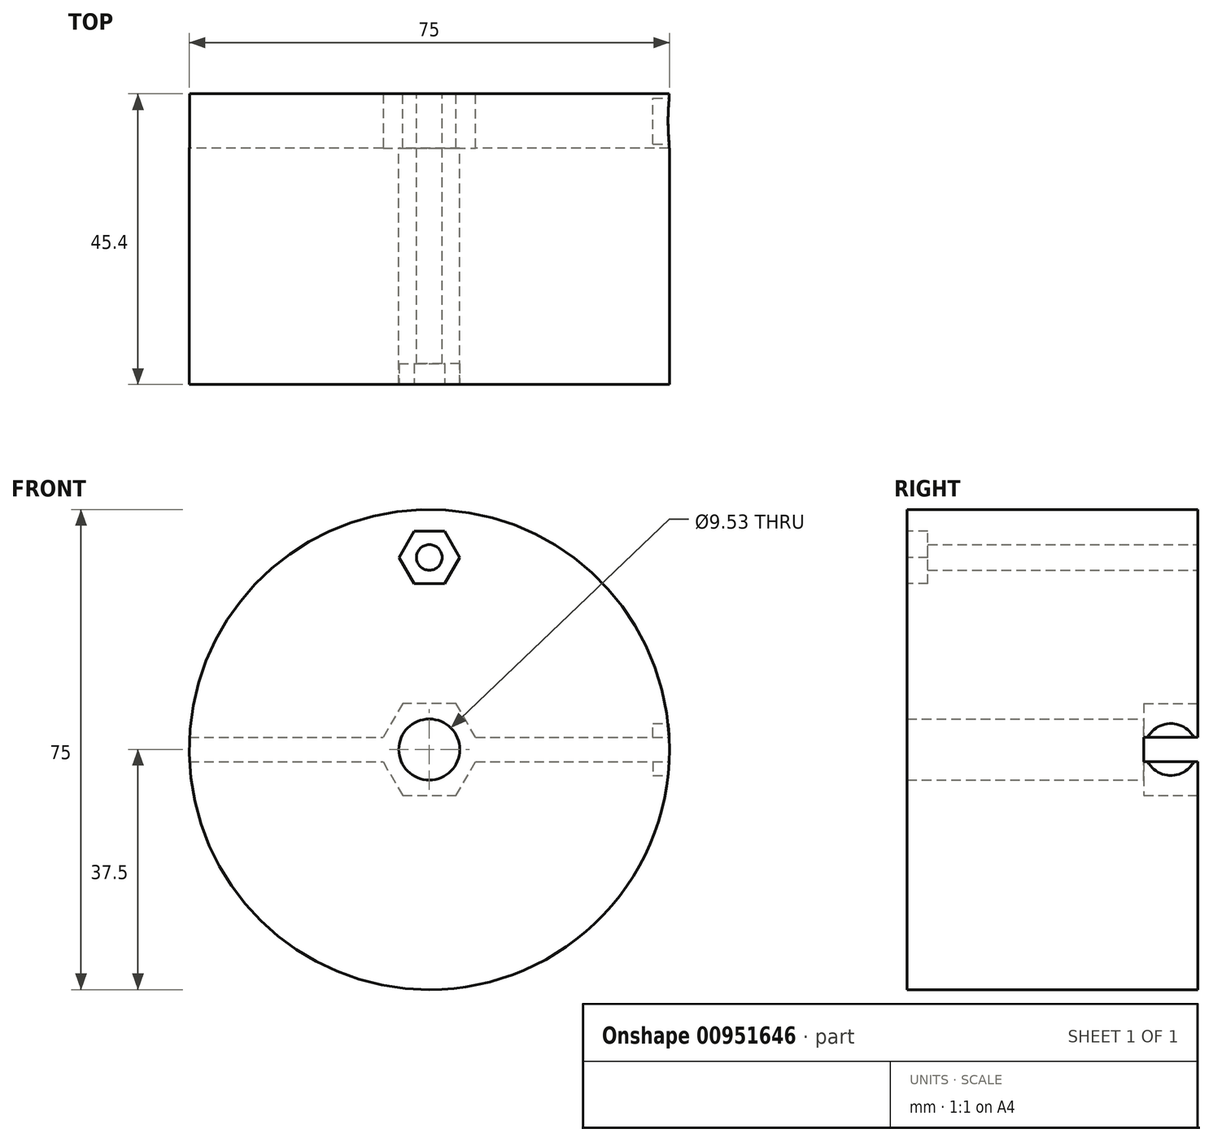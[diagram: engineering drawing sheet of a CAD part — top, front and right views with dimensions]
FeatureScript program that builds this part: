
annotation { "Feature Type Name" : "Feature", "Feature Type Description" : "" }
export const myFeature = defineFeature(function(context is Context, id is Id, definition is map)
    precondition{}
    {
        {
            var Q0;
            Q0=qCreatedBy(makeId("Front.planeOp"),FACE);
            var sketch = newSketch(context, id + "F0", { "sketchPlane" : qUnion([Q0])});
            skCircle(sketch, "E0", {"center": v(0, 0) * mm, "radius": 37.5 * mm});
            skSolve(sketch);
        }
        {
            var Q0;
            Q0=qSketchRegion(id+"F0",true);
            extrude(context, id + "F1", {"entities" : qUnion([Q0]), "depth" : 45.4 * mm, "offsetDistance" : 25 * mm});
        }
        {
            var Q0;
            Q0=qCreatedBy(makeId("Front.planeOp"),FACE);
            var sketch = newSketch(context, id + "F2", { "sketchPlane" : qUnion([Q0])});
            skCircle(sketch, "E1", {"center": v(0, 30) * mm, "radius": 2 * mm});
            skSolve(sketch);
        }
        {
            var Q0;
            Q0=qSketchRegion(id+"F2",true);
            extrude(context, id + "F3", {"entities" : qUnion([Q0]), "operationType" : NewBodyOperationType.REMOVE, "endBound" : BoundingType.THROUGH_ALL, "depth" : 25 * mm, "offsetDistance" : 25 * mm});
        }
        {
            var Q0;
            Q0=makeQuery(id+"F1.opExtrude","CAP_FACE",FACE,{"disambiguationData":[OSD([sQuery(id+"F0.wireOp",EDGE,"E0")])],"isStart":false});
            var sketch = newSketch(context, id + "F4", { "sketchPlane" : qUnion([Q0])});
            skCircle(sketch, "E2.cCircle", {"center": v(0, 30) * mm, "radius": 4.11 * mm, "construction": true});
            skLineSegment(sketch, "E2.0", {"start": v(-2.37, 34.11) * mm, "end": v(2.37, 34.11) * mm});
            skLineSegment(sketch, "E2.1", {"start": v(2.37, 34.11) * mm, "end": v(4.75, 30) * mm});
            skLineSegment(sketch, "E2.2", {"start": v(4.75, 30) * mm, "end": v(2.37, 25.89) * mm});
            skLineSegment(sketch, "E2.3", {"start": v(2.37, 25.89) * mm, "end": v(-2.37, 25.89) * mm});
            skLineSegment(sketch, "E2.4", {"start": v(-2.37, 25.89) * mm, "end": v(-4.75, 30) * mm});
            skLineSegment(sketch, "E2.5", {"start": v(-4.75, 30) * mm, "end": v(-2.37, 34.11) * mm});
            skPoint(sketch, "E2.0.midPoint", {"position": v(0, 34.11) * mm});
            skSolve(sketch);
        }
        {
            var Q0;
            Q0=qSketchRegion(id+"F4",true);
            extrude(context, id + "F5", {"entities" : qUnion([Q0]), "operationType" : NewBodyOperationType.REMOVE, "oppositeDirection" : true, "depth" : 3.25 * mm, "offsetDistance" : 25 * mm});
        }
        {
            var Q0;
            Q0=makeQuery(id+"F1.opExtrude","CAP_FACE",FACE,{"disambiguationData":[OSD([sQuery(id+"F0.wireOp",EDGE,"E0")])],"isStart":true});
            var sketch = newSketch(context, id + "F6", { "sketchPlane" : qUnion([Q0])});
            skCircle(sketch, "E3.cCircle", {"center": v(0, 0) * mm, "radius": 7.2 * mm, "construction": true});
            skLineSegment(sketch, "E3.0", {"start": v(4.16, -7.2) * mm, "end": v(-4.16, -7.2) * mm});
            skLineSegment(sketch, "E3.1", {"start": v(-4.16, -7.2) * mm, "end": v(-8.31, 0) * mm});
            skLineSegment(sketch, "E3.2", {"start": v(-8.31, 0) * mm, "end": v(-4.16, 7.2) * mm});
            skLineSegment(sketch, "E3.3", {"start": v(-4.16, 7.2) * mm, "end": v(4.16, 7.2) * mm});
            skLineSegment(sketch, "E3.4", {"start": v(4.16, 7.2) * mm, "end": v(8.31, 0) * mm});
            skLineSegment(sketch, "E3.5", {"start": v(8.31, 0) * mm, "end": v(4.16, -7.2) * mm});
            skPoint(sketch, "E3.0.midPoint", {"position": v(0, -7.2) * mm});
            skSolve(sketch);
        }
        {
            var Q0;
            Q0=qSketchRegion(id+"F6",true);
            extrude(context, id + "F7", {"entities" : qUnion([Q0]), "operationType" : NewBodyOperationType.REMOVE, "oppositeDirection" : true, "depth" : 8.46 * mm, "offsetDistance" : 25 * mm});
        }
        {
            var Q0;
            Q0=makeQuery(id+"F1.opExtrude","CAP_FACE",FACE,{"disambiguationData":[OSD([sQuery(id+"F0.wireOp",EDGE,"E0")])],"isStart":true});
            var sketch = newSketch(context, id + "F8", { "sketchPlane" : qUnion([Q0])});
            skLineSegment(sketch, "E4.bottom", {"start": v(38.1, 1.9) * mm, "end": v(-38.1, 1.9) * mm});
            skLineSegment(sketch, "E4.top", {"start": v(38.1, -1.9) * mm, "end": v(-38.1, -1.9) * mm});
            skLineSegment(sketch, "E4.left", {"start": v(38.1, 1.9) * mm, "end": v(38.1, -1.9) * mm});
            skLineSegment(sketch, "E4.right", {"start": v(-38.1, 1.9) * mm, "end": v(-38.1, -1.9) * mm});
            skPoint(sketch, "E4.middle", {"position": v(0, 0) * mm});
            skSolve(sketch);
        }
        {
            var Q0;
            Q0=qSketchRegion(id+"F8",true);
            var Q1;
            Q1=makeQuery(id+"F7.boolean.opBoolean","COPY",FACE,{"derivedFrom":makeQuery(id+"F7.opExtrude","CAP_FACE",FACE,{"disambiguationData":[OSD([sQuery(id+"F6.wireOp",EDGE,"E3.0"),sQuery(id+"F6.wireOp",EDGE,"E3.1"),sQuery(id+"F6.wireOp",EDGE,"E3.2"),sQuery(id+"F6.wireOp",EDGE,"E3.3"),sQuery(id+"F6.wireOp",EDGE,"E3.4"),sQuery(id+"F6.wireOp",EDGE,"E3.5")])],"isStart":false})});
            extrude(context, id + "F9", {"entities" : qUnion([Q0]), "operationType" : NewBodyOperationType.REMOVE, "endBound" : BoundingType.UP_TO_SURFACE, "oppositeDirection" : true, "depth" : 25 * mm, "endBoundEntityFace" : qUnion([Q1]), "offsetDistance" : 25 * mm});
        }
        {
            var Q0;
            {var subQ0=sQuery(id+"F8.wireOp",EDGE,"E4.top");Q0=makeQuery(id+"F9.boolean.opBoolean","INTERSECT",VERTEX,{"disambiguationData":[OD(0.0)],"derivedFrom":[makeQuery(id+"F1.opExtrude","SWEPT_FACE",FACE,{"disambiguationData":[OSD([sQuery(id+"F0.wireOp",EDGE,"E0")])]}),makeQuery(id+"F9.opExtrude","CAP_FACE",FACE,{"disambiguationData":[OSD([sQuery(id+"F8.wireOp",EDGE,"E4.bottom"),subQ0,sQuery(id+"F8.wireOp",EDGE,"E4.left"),sQuery(id+"F8.wireOp",EDGE,"E4.right")])],"isStart":false}),makeQuery(id+"F9.opExtrude","SWEPT_FACE",FACE,{"disambiguationData":[OSD([subQ0])]})]});}
            var Q1;
            {var subQ0=sQuery(id+"F8.wireOp",EDGE,"E4.bottom");Q1=makeQuery(id+"F9.boolean.opBoolean","INTERSECT",VERTEX,{"disambiguationData":[OD(0.0)],"derivedFrom":[makeQuery(id+"F1.opExtrude","SWEPT_FACE",FACE,{"disambiguationData":[OSD([sQuery(id+"F0.wireOp",EDGE,"E0")])]}),makeQuery(id+"F9.opExtrude","SWEPT_FACE",FACE,{"disambiguationData":[OSD([subQ0])]}),makeQuery(id+"F9.opExtrude","CAP_FACE",FACE,{"disambiguationData":[OSD([subQ0,sQuery(id+"F8.wireOp",EDGE,"E4.top"),sQuery(id+"F8.wireOp",EDGE,"E4.left"),sQuery(id+"F8.wireOp",EDGE,"E4.right")])],"isStart":false})]});}
            var Q2;
            Q2=makeQuery(id+"F9.boolean.opBoolean","INTERSECT",VERTEX,{"disambiguationData":[OD(0.0)],"derivedFrom":[makeQuery(id+"F1.opExtrude","SWEPT_FACE",FACE,{"disambiguationData":[OSD([sQuery(id+"F0.wireOp",EDGE,"E0")])]}),makeQuery(id+"F9.opExtrude","SWEPT_FACE",FACE,{"disambiguationData":[OSD([sQuery(id+"F8.wireOp",EDGE,"E4.bottom")])]})]});
            cPlane(context, id + "F10", {"entities" : qUnion([Q0, Q1, Q2]), "cplaneType" : CPlaneType.THREE_POINT, "offset" : 25.4 * mm, "width" : 152.4 * mm, "height" : 152.4 * mm});
        }
        {
            var Q0;
            Q0=qCreatedBy(id+"F10.planeOp",FACE);
            var sketch = newSketch(context, id + "F11", { "sketchPlane" : qUnion([Q0])});
            skCircle(sketch, "E5", {"center": v(-4.23, 0) * mm, "radius": 4.06 * mm});
            skCircle(sketch, "E6", {"center": v(-4.23, 0) * mm, "radius": 1.9 * mm, "construction": true});
            skLineSegment(sketch, "E7", {"start": v(-4.23, 0) * mm, "end": v(-4.23, -1.9) * mm, "construction": true});
            skSolve(sketch);
        }
        {
            var Q0;
            Q0 = qSketchRegion(id + "F11", true);
            extrude(context, id + "F12", {"entities" : qUnion([Q0]), "operationType" : NewBodyOperationType.REMOVE, "oppositeDirection" : true, "depth" : 2.54 * mm, "offsetDistance" : 25.4 * mm});
        }
        {
            var Q0;
            Q0=makeQuery(id+"F9.boolean.opBoolean","MERGE",FACE,{"derivedFrom":[makeQuery(id+"FiCGK556RHEn4Ie_1.boolean.opBoolean","COPY",FACE,{"derivedFrom":makeQuery(id+"FiCGK556RHEn4Ie_1.opExtrude","CAP_FACE",FACE,{"disambiguationData":[OSD([sQuery(id+"Fi5u4YFzBx5e4HE_1.wireOp",EDGE,"ob4QSSdM-Jolo-ZbyU-Ib3B-bAmZaLx6JoKU.bottom"),sQuery(id+"Fi5u4YFzBx5e4HE_1.wireOp",EDGE,"ob4QSSdM-Jolo-ZbyU-Ib3B-bAmZaLx6JoKU.top"),sQuery(id+"Fi5u4YFzBx5e4HE_1.wireOp",EDGE,"ob4QSSdM-Jolo-ZbyU-Ib3B-bAmZaLx6JoKU.left"),sQuery(id+"Fi5u4YFzBx5e4HE_1.wireOp",EDGE,"ob4QSSdM-Jolo-ZbyU-Ib3B-bAmZaLx6JoKU.right")])],"isStart":false})})],"fromTools":[makeQuery(id+"F9.opExtrude","CAP_FACE",FACE,{"disambiguationData":[OSD([sQuery(id+"F8.wireOp",EDGE,"E4.bottom"),sQuery(id+"F8.wireOp",EDGE,"E4.top"),sQuery(id+"F8.wireOp",EDGE,"E4.left"),sQuery(id+"F8.wireOp",EDGE,"E4.right")])],"isStart":false})]});
            var sketch = newSketch(context, id + "F13", { "sketchPlane" : qUnion([Q0])});
            skCircle(sketch, "E8", {"center": v(0, 0) * mm, "radius": 4.76 * mm});
            skSolve(sketch);
        }
        {
            var Q0;
            Q0=qSketchRegion(id+"F13",true);
            extrude(context, id + "F14", {"entities" : qUnion([Q0]), "operationType" : NewBodyOperationType.REMOVE, "endBound" : BoundingType.THROUGH_ALL, "oppositeDirection" : true, "depth" : 25 * mm, "offsetDistance" : 25 * mm});
        }
    });
